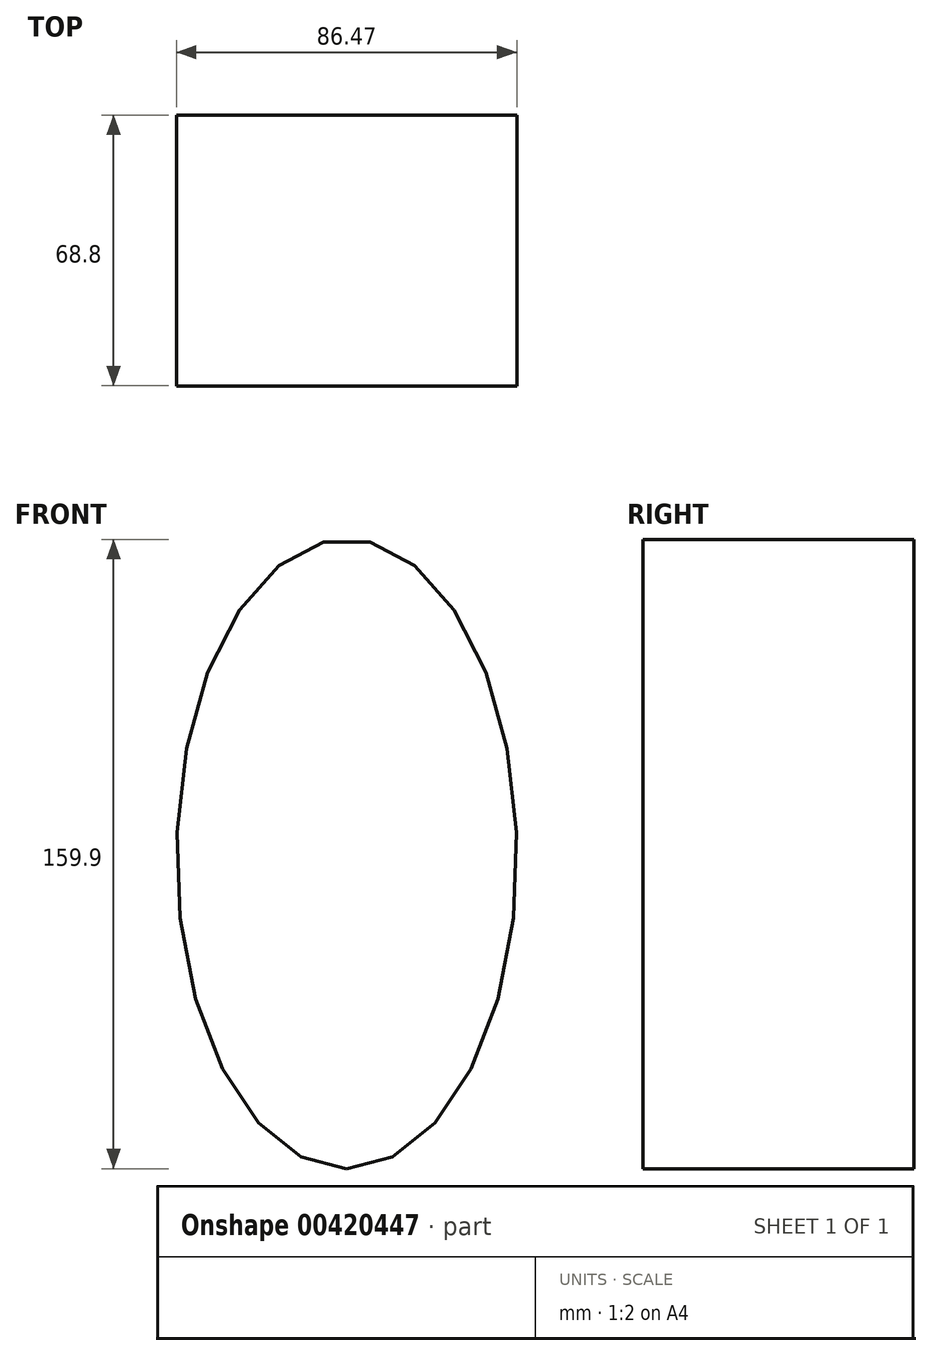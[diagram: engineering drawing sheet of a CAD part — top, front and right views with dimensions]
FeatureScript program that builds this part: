
annotation { "Feature Type Name" : "Feature", "Feature Type Description" : "" }
export const myFeature = defineFeature(function(context is Context, id is Id, definition is map)
    precondition{}
    {
        {
            var Q0;
            Q0=qCreatedBy(makeId("Front.planeOp"),FACE);
            var sketch = newSketch(context, id + "F0", { "sketchPlane" : qUnion([Q0])});
            skEllipse(sketch, "E0", {"center": v(10.98, 142.34) * mm, "majorRadius": 79.95 * mm, "minorRadius": 43.23 * mm, "majorAxis": v(0, -1)});
            skSolve(sketch);
        }
        {
            var Q0;
            Q0=makeQuery(id+"F0.imprint","IMPRINT",FACE,{"disambiguationData":[TD([[makeQuery(id+"F0.imprint","IMPRINT",EDGE,{"derivedFrom":sQuery(id+"F0.wireOp",EDGE,"E0")}),1.0]])]});
            extrude(context, id + "F1", {"entities" : qUnion([Q0]), "depth" : 68.8 * mm});
        }
    });
